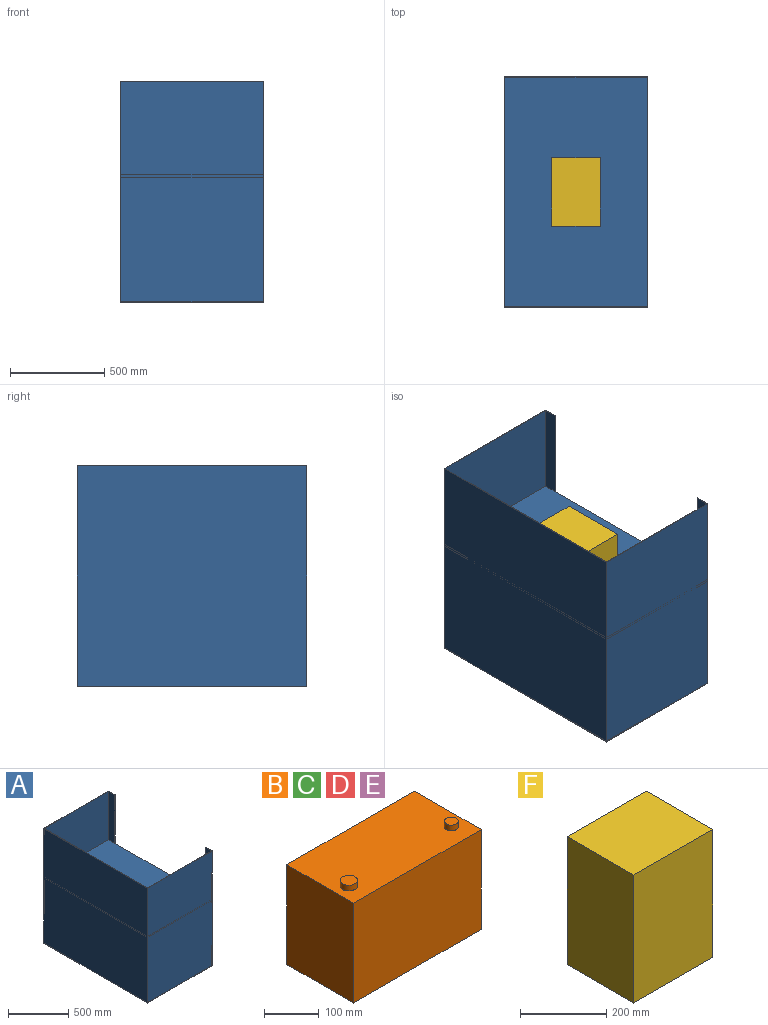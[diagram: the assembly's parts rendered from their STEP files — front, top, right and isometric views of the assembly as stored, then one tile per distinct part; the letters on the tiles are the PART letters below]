
ASSEMBLY  parts=6 mates=5
PART A: 22 faces, bbox 762x1219.2x1168.4 mm
  f0: plane 755.65x660.4mm, normal (0,-1,0), area 499031.3mm2, adj f2,f3,f15,f21
  f1: plane 755.65x660.4mm, normal (0,1,0), area 499031.3mm2, adj f2,f3,f15,f21
  f2: plane 1212.85x660.4mm, normal (1,0,0), area 800966.1mm2, adj f0,f1,f15,f21
  f3: plane 1212.85x660.4mm, normal (-1,0,0), area 716288.9mm2, adj f0,f1,f15,f16,f17,f18,f21
  f4: plane 492.13x73.03mm, normal (-1,0,0), area 35937.4mm2, adj f7,f8,f18,f20
  f5: plane 492.13x73.03mm, normal (-1,0,0), area 35937.4mm2, adj f7,f9,f17,f20
  f6: plane 1219.2x1168.4mm, normal (1,0,0), area 801288.7mm2, adj f7,f10,f12,f14,f16,f17,f18
  f7: plane 1219.2x762mm, normal (0,0,1), area 9153.2mm2, adj f4,f5,f6,f8,f9,f10,f11,f12
  f8: plane 755.65x492.13mm, normal (0,-1,0), area 371874.3mm2, adj f4,f7,f13,f20
  f9: plane 755.65x492.13mm, normal (0,1,0), area 371874.3mm2, adj f5,f7,f13,f20
  f10: plane 1168.4x762mm, normal (0,1,0), area 890320.8mm2, adj f6,f7,f11,f14
  f11: plane 1219.2x1168.4mm, normal (-1,0,0), area 1424513.3mm2, adj f7,f10,f12,f14
  f12: plane 1168.4x762mm, normal (0,-1,0), area 890320.8mm2, adj f6,f7,f11,f14
  f13: plane 1212.85x492.13mm, normal (1,0,0), area 596873.8mm2, adj f7,f8,f9,f20
  f14: plane 1219.2x762mm, normal (0,0,-1), area 929030.4mm2, adj f6,f10,f11,f12
  f15: plane 1212.85x755.65mm, normal (0,0,1), area 916490.1mm2, adj f0,f1,f2,f3
  f16: plane 1066.8x3.18mm, normal (0,0,1), area 3387.1mm2, adj f3,f6,f17,f18
  f17: plane 584.2x3.18mm, normal (0,1,0), area 1854.8mm2, adj f3,f5,f6,f7,f16,f19
  f18: plane 584.2x3.18mm, normal (0,-1,0), area 1854.8mm2, adj f3,f4,f6,f7,f16,f19
  f19: plane 1066.8x12.7mm, normal (1,0,0), area 13548.4mm2, adj f17,f18,f20,f21
  f20: plane 1212.85x755.65mm, normal (0,0,1), area 916490.1mm2, adj f4,f5,f8,f9,f13,f19
  f21: plane 1212.85x755.65mm, normal (0,0,-1), area 916490.1mm2, adj f0,f1,f2,f3,f19
PART B: 10 faces, bbox 330.2x172.7x236.2 mm
  f0: plane 223.52x172.72mm, normal (1,0,0), area 38606.4mm2, adj f1,f3,f4,f5
  f1: plane 330.2x223.52mm, normal (0,1,0), area 73806.3mm2, adj f0,f2,f4,f5
  f2: plane 223.52x172.72mm, normal (-1,0,0), area 38606.4mm2, adj f1,f3,f4,f5
  f3: plane 330.2x223.52mm, normal (0,-1,0), area 73806.3mm2, adj f0,f2,f4,f5
  f4: plane 330.2x172.72mm, normal (0,0,1), area 55733.7mm2, adj f0,f1,f2,f3,f6,f8
  f5: plane 330.2x172.72mm, normal (0,0,-1), area 57032.1mm2, adj f0,f1,f2,f3
  f6: cylinder r=15.88mm len=31.75mm, axis (0,0,-1), area 1266.8mm2, adj f4,f7
  f7: plane 31.75x31.75mm, normal (0,0,1), area 791.7mm2, adj f6
  f8: cylinder r=12.7mm len=25.4mm, axis (0,0,-1), area 1013.4mm2, adj f4,f9
  f9: plane 25.4x25.4mm, normal (0,0,1), area 506.7mm2, adj f8
PART C: same geometry as B
PART D: same geometry as B
PART E: same geometry as B
PART F: 6 faces, bbox 259.1x218.4x363.2 mm
  f0: plane 363.22x259.08mm, normal (0,-1,0), area 94103mm2, adj f1,f3,f4,f5
  f1: plane 363.22x218.44mm, normal (1,0,0), area 79341.8mm2, adj f0,f2,f4,f5
  f2: plane 363.22x259.08mm, normal (0,1,0), area 94103mm2, adj f1,f3,f4,f5
  f3: plane 363.22x218.44mm, normal (-1,0,0), area 79341.8mm2, adj f0,f2,f4,f5
  f4: plane 259.08x218.44mm, normal (0,0,1), area 56593.4mm2, adj f0,f1,f2,f3
  f5: plane 259.08x218.44mm, normal (0,0,-1), area 56593.4mm2, adj f0,f1,f2,f3
PLACE A t=(-203.59,219.13,-52.54)mm fixed
PLACE B rot(axis=(0,0,1),90deg) t=(-305.65,446.64,-49.36)mm
PLACE C rot(axis=(0,0,1),90deg) t=(-297.96,71.06,-49.36)mm
PLACE D rot(axis=(0,0,-1),90deg) t=(-64.52,443.27,-49.36)mm
PLACE E rot(axis=(0,0,-1),90deg) t=(-63.67,32.28,-49.36)mm
PLACE F rot(axis=(-1,0,0),90deg) t=(-203.59,37.52,720.26)mm
MATE planar D.f5 <-> A.f15  axis (0,0,-1) through (-64.52,443.27,-49.36)mm
MATE planar F.f2 <-> A.f21  axis (0,0,-1) through (-203.59,219.13,611.04)mm
MATE planar B.f5 <-> A.f15  axis (0,0,-1) through (-305.65,446.64,-49.36)mm
MATE planar E.f5 <-> A.f15  axis (0,0,-1) through (-63.67,32.28,-49.36)mm
MATE planar C.f5 <-> A.f15  axis (0,0,-1) through (-297.96,71.06,-49.36)mm
